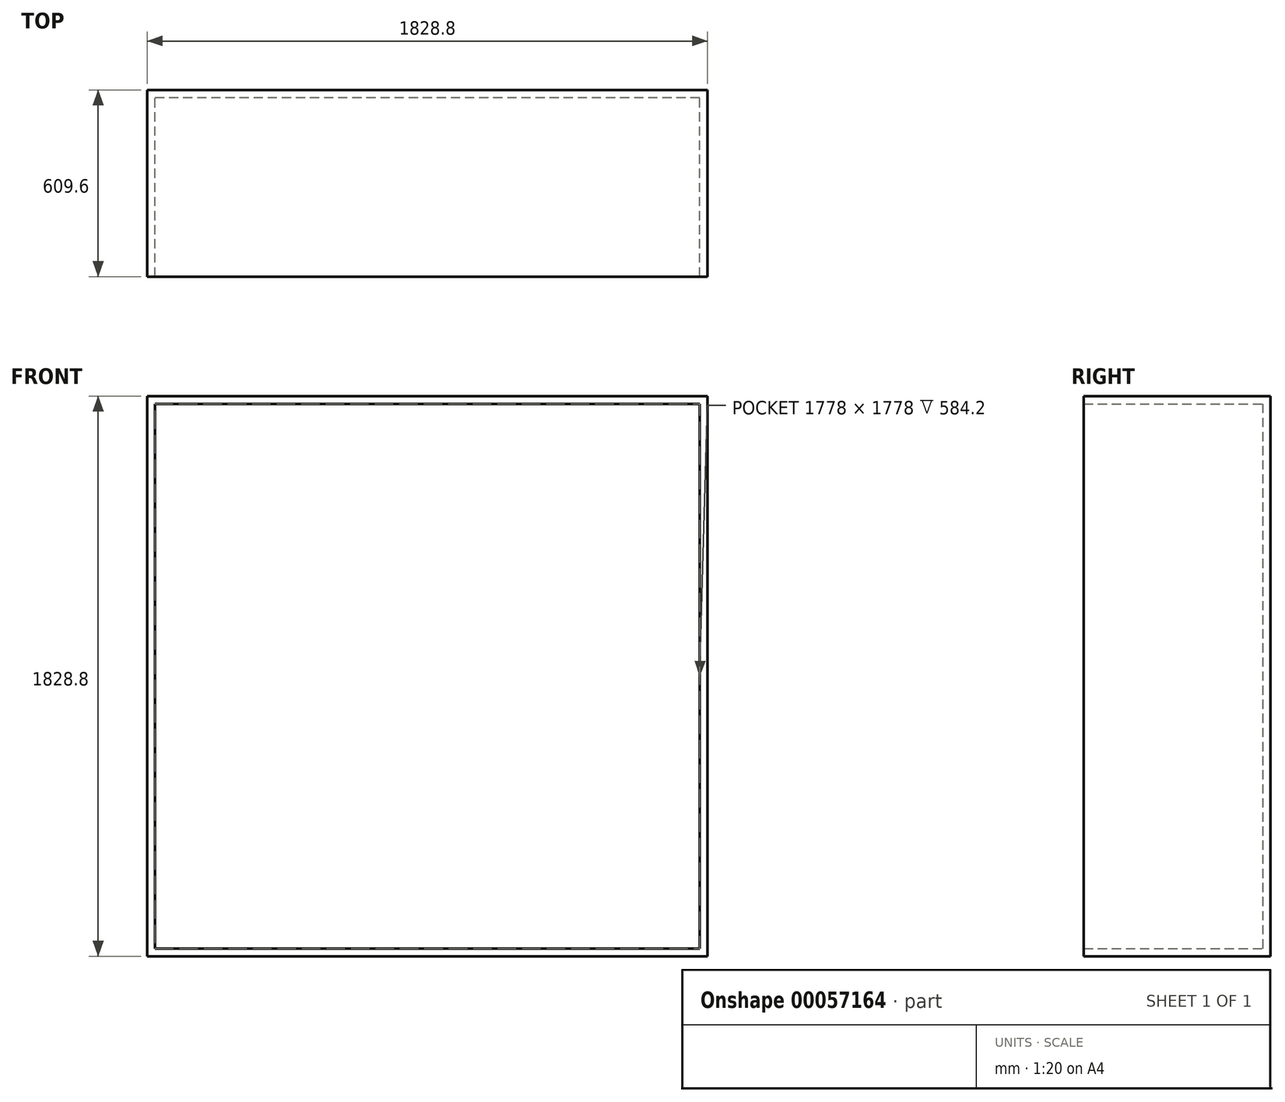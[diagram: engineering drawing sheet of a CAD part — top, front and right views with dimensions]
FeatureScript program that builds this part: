
annotation { "Feature Type Name" : "Feature", "Feature Type Description" : "" }
export const myFeature = defineFeature(function(context is Context, id is Id, definition is map)
    precondition{}
    {
        {
            var Q0;
            Q0=qCreatedBy(makeId("Top.planeOp"),FACE);
            var sketch = newSketch(context, id + "F0", { "sketchPlane" : qUnion([Q0])});
            skLineSegment(sketch, "E0.rect.bottom", {"start": v(914.4, -304.8) * mm, "end": v(-914.4, -304.8) * mm});
            skLineSegment(sketch, "E0.rect.top", {"start": v(914.4, 304.8) * mm, "end": v(-914.4, 304.8) * mm});
            skLineSegment(sketch, "E0.rect.left", {"start": v(914.4, -304.8) * mm, "end": v(914.4, 304.8) * mm});
            skLineSegment(sketch, "E0.rect.right", {"start": v(-914.4, -304.8) * mm, "end": v(-914.4, 304.8) * mm});
            skPoint(sketch, "E0.rect.middle", {"position": v(0, 0) * mm});
            skSolve(sketch);
        }
        {
            var Q0;
            Q0=makeQuery(id+"F0.imprint","IMPRINT",FACE,{"disambiguationData":[TD([[makeQuery(id+"F0.imprint","IMPRINT",EDGE,{"derivedFrom":sQuery(id+"F0.wireOp",EDGE,"E0.rect.bottom")}),-1.0]])]});
            extrude(context, id + "F1", {"entities" : qUnion([Q0]), "depth" : 1828.8 * mm});
        }
        {
            var Q0;
            Q0=makeQuery(id+"F1.opExtrude","SWEPT_FACE",FACE,{"disambiguationData":[OSD([sQuery(id+"F0.wireOp",EDGE,"E0.rect.bottom")])]});
            shell(context, id + "F2", {"entities" : qUnion([Q0]), "thickness" : 25.4 * mm});
        }
    });
